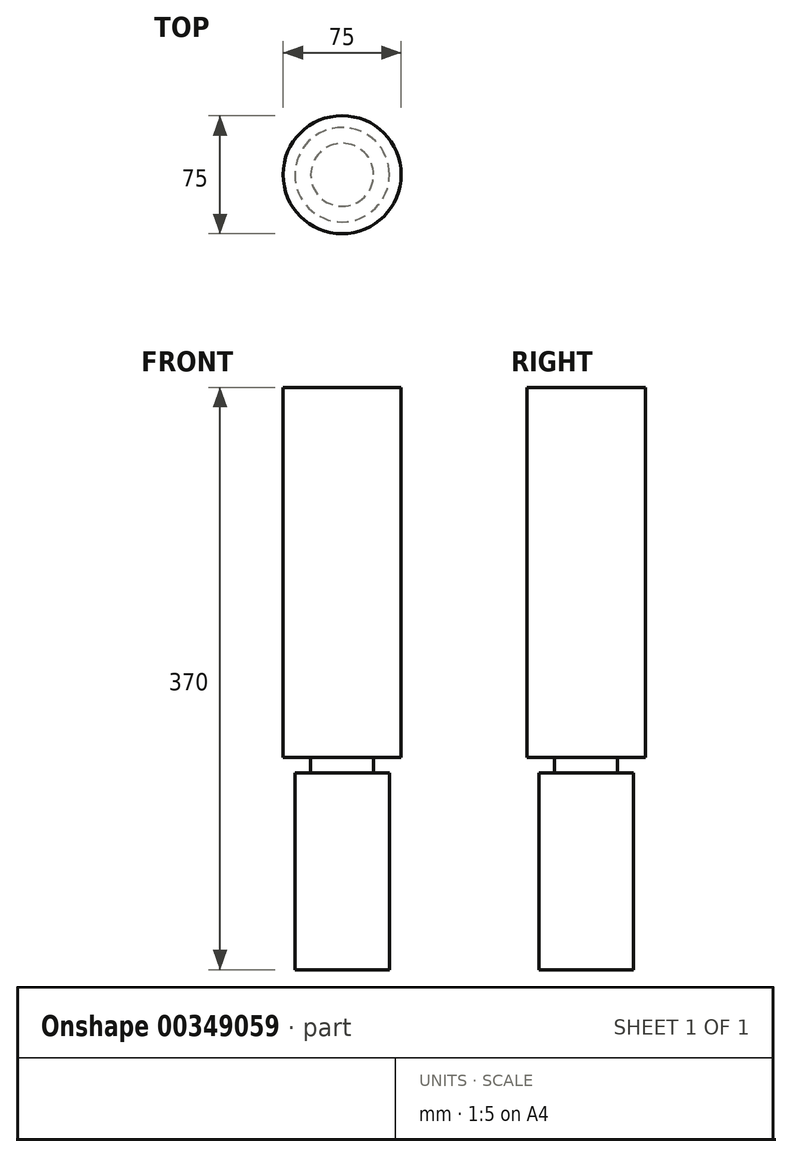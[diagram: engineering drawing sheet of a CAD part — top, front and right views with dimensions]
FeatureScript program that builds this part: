
annotation { "Feature Type Name" : "Feature", "Feature Type Description" : "" }
export const myFeature = defineFeature(function(context is Context, id is Id, definition is map)
    precondition{}
    {
        {
            var Q0;
            Q0=qCreatedBy(makeId("Top.planeOp"),FACE);
            var sketch = newSketch(context, id + "F0", { "sketchPlane" : qUnion([Q0])});
            skCircle(sketch, "E0", {"center": v(0, 0) * mm, "radius": 30 * mm});
            skSolve(sketch);
        }
        {
            var Q0;
            Q0 = qSketchRegion(id + "F0", true);
            extrude(context, id + "F1", {"entities" : qUnion([Q0]), "depth" : 125 * mm, "offsetDistance" : 25 * mm});
        }
        {
            var Q0;
            Q0=makeQuery(id+"F1.opExtrude","CAP_FACE",FACE,{"disambiguationData":[OSD([sQuery(id+"F0.wireOp",EDGE,"E0")])],"isStart":false});
            var sketch = newSketch(context, id + "F2", { "sketchPlane" : qUnion([Q0])});
            skCircle(sketch, "E1", {"center": v(0, 0) * mm, "radius": 20 * mm});
            skSolve(sketch);
        }
        {
            var Q0;
            Q0 = qSketchRegion(id + "F2", true);
            extrude(context, id + "F3", {"entities" : qUnion([Q0]), "operationType" : NewBodyOperationType.ADD, "depth" : 10 * mm, "offsetDistance" : 25 * mm});
        }
        {
            var Q0;
            Q0=makeQuery(id+"F3.opExtrude","CAP_FACE",FACE,{"disambiguationData":[OSD([sQuery(id+"F2.wireOp",EDGE,"E1")])],"isStart":false});
            var sketch = newSketch(context, id + "F4", { "sketchPlane" : qUnion([Q0])});
            skCircle(sketch, "E2", {"center": v(0, 0) * mm, "radius": 37.5 * mm});
            skSolve(sketch);
        }
        {
            var Q0;
            Q0 = qSketchRegion(id + "F4", true);
            extrude(context, id + "F5", {"entities" : qUnion([Q0]), "operationType" : NewBodyOperationType.ADD, "depth" : 235 * mm, "offsetDistance" : 25 * mm});
        }
    });
